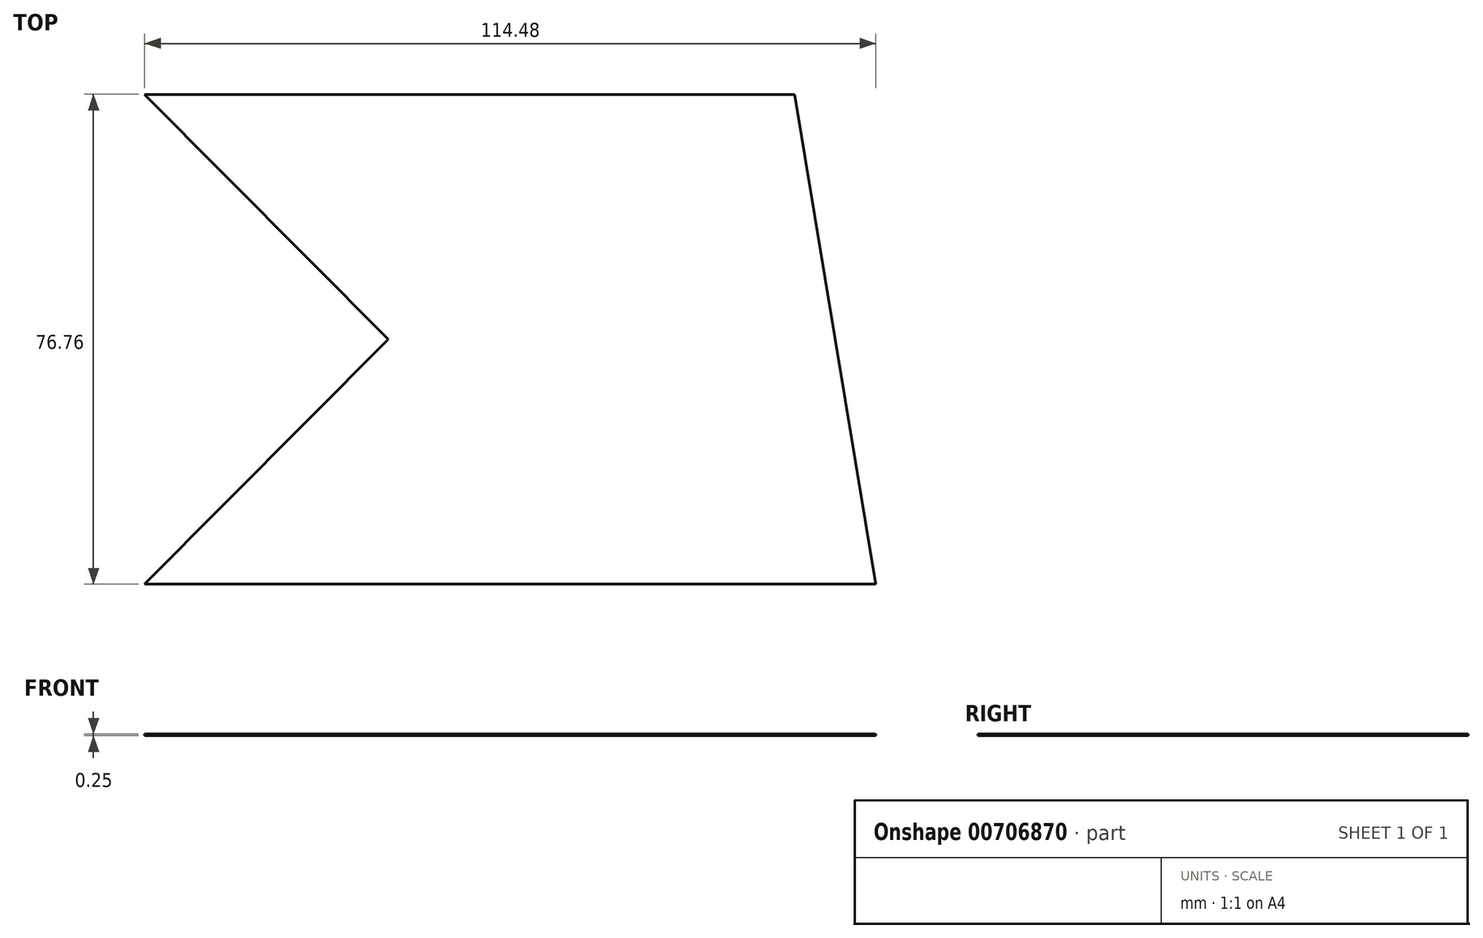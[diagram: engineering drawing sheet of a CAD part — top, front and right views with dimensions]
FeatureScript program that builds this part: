
annotation { "Feature Type Name" : "Feature", "Feature Type Description" : "" }
export const myFeature = defineFeature(function(context is Context, id is Id, definition is map)
    precondition{}
    {
        {
            var Q0;
            Q0=qCreatedBy(makeId("Top.planeOp"),FACE);
            var sketch = newSketch(context, id + "F0", { "sketchPlane" : qUnion([Q0])});
            skLineSegment(sketch, "E0", {"start": v(-6.27, -8.78) * mm, "end": v(-44.43, 29.6) * mm});
            skLineSegment(sketch, "E1", {"start": v(-6.27, -8.78) * mm, "end": v(-44.43, -47.16) * mm});
            skLineSegment(sketch, "E2", {"start": v(57.36, 29.6) * mm, "end": v(70.05, -47.16) * mm});
            skLineSegment(sketch, "E3", {"start": v(-44.43, 29.6) * mm, "end": v(57.36, 29.6) * mm});
            skLineSegment(sketch, "E4", {"start": v(-44.43, -47.16) * mm, "end": v(70.05, -47.16) * mm});
            skSolve(sketch);
        }
        {
            var Q0;
            Q0 = qSketchRegion(id + "F0", true);
            extrude(context, id + "F1", {"entities" : qUnion([Q0]), "depth" : 0.25 * mm, "offsetDistance" : 25.4 * mm});
        }
    });
